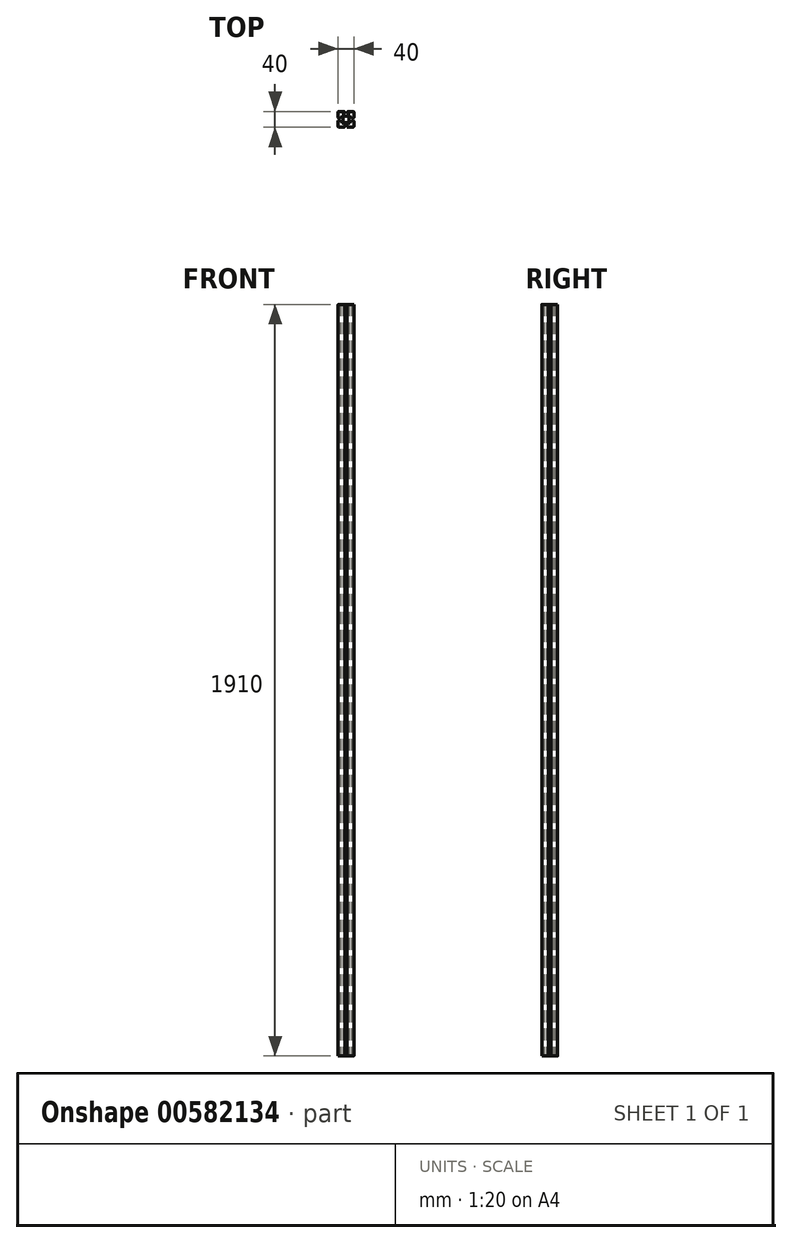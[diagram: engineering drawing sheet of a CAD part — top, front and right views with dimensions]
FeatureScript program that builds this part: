
annotation { "Feature Type Name" : "Feature", "Feature Type Description" : "" }
export const myFeature = defineFeature(function(context is Context, id is Id, definition is map)
    precondition{}
    {
        {
            var Q0;
            Q0=qCreatedBy(makeId("Top.planeOp"),FACE);
            var sketch = newSketch(context, id + "F0", { "sketchPlane" : qUnion([Q0])});
            skLineSegment(sketch, "E0.bottom", {"start": v(20, 20) * mm, "end": v(3, 20) * mm});
            skLineSegment(sketch, "E0.top", {"start": v(20, -20) * mm, "end": v(3, -20) * mm});
            skLineSegment(sketch, "E0.left", {"start": v(20, 20) * mm, "end": v(20, 3) * mm});
            skLineSegment(sketch, "E0.right", {"start": v(-20, 20) * mm, "end": v(-20, 3) * mm});
            skPoint(sketch, "E0.middle", {"position": v(0, 0) * mm});
            skLineSegment(sketch, "E1.left", {"start": v(3, 14) * mm, "end": v(3, 20) * mm});
            skLineSegment(sketch, "E1.right", {"start": v(-3, 14) * mm, "end": v(-3, 20) * mm});
            skPoint(sketch, "E1.middle", {"position": v(0, 20) * mm});
            skLineSegment(sketch, "E2.bottom", {"start": v(-6, 14) * mm, "end": v(-3, 14) * mm});
            skLineSegment(sketch, "E2.top", {"start": v(-6, 8) * mm, "end": v(6, 8) * mm});
            skLineSegment(sketch, "E2.left", {"start": v(-6, 14) * mm, "end": v(-6, 8) * mm});
            skLineSegment(sketch, "E2.right", {"start": v(6, 14) * mm, "end": v(6, 8) * mm});
            skPoint(sketch, "E2.middle", {"position": v(0, 11) * mm});
            skLineSegment(sketch, "E3.bottom", {"start": v(14, 3) * mm, "end": v(20, 3) * mm});
            skLineSegment(sketch, "E3.top", {"start": v(14, -3) * mm, "end": v(20, -3) * mm});
            skPoint(sketch, "E3.middle", {"position": v(20, 0) * mm});
            skLineSegment(sketch, "E4.bottom", {"start": v(14, 6) * mm, "end": v(8, 6) * mm});
            skLineSegment(sketch, "E4.top", {"start": v(14, -6) * mm, "end": v(8, -6) * mm});
            skLineSegment(sketch, "E4.left", {"start": v(14, 6) * mm, "end": v(14, 3) * mm});
            skLineSegment(sketch, "E4.right", {"start": v(8, 6) * mm, "end": v(8, -6) * mm});
            skPoint(sketch, "E4.middle", {"position": v(11, 0) * mm});
            skPoint(sketch, "E4.middle.positionSnap0", {"position": v(14, 0) * mm});
            skPoint(sketch, "E4.centerSnap0", {"position": v(14, 0) * mm});
            skLineSegment(sketch, "E5.left", {"start": v(3.1, -14) * mm, "end": v(3, -20) * mm});
            skLineSegment(sketch, "E5.right", {"start": v(-2.9, -14) * mm, "end": v(-3, -20) * mm});
            skPoint(sketch, "E5.middle", {"position": v(0, -20) * mm});
            skLineSegment(sketch, "E6.bottom", {"start": v(6, -14) * mm, "end": v(3.1, -14) * mm});
            skLineSegment(sketch, "E6.top", {"start": v(6, -8) * mm, "end": v(-6, -8) * mm});
            skLineSegment(sketch, "E6.left", {"start": v(6, -14) * mm, "end": v(6, -8) * mm});
            skLineSegment(sketch, "E6.right", {"start": v(-6, -14) * mm, "end": v(-6, -8) * mm});
            skPoint(sketch, "E6.middle", {"position": v(0, -11) * mm});
            skLineSegment(sketch, "E7.bottom", {"start": v(-14, -3) * mm, "end": v(-20, -3) * mm});
            skLineSegment(sketch, "E7.top", {"start": v(-14, 3) * mm, "end": v(-20, 3) * mm});
            skPoint(sketch, "E7.middle", {"position": v(-20, 0) * mm});
            skLineSegment(sketch, "E8.bottom", {"start": v(-14, 6) * mm, "end": v(-8, 6) * mm});
            skLineSegment(sketch, "E8.top", {"start": v(-14, -6) * mm, "end": v(-8, -6) * mm});
            skLineSegment(sketch, "E8.left", {"start": v(-14, 6) * mm, "end": v(-14, 3) * mm});
            skLineSegment(sketch, "E8.right", {"start": v(-8, 6) * mm, "end": v(-8, -6) * mm});
            skPoint(sketch, "E8.middle", {"position": v(-11, 0) * mm});
            skPoint(sketch, "E8.cornerSnap0", {"position": v(-14, 0) * mm});
            skPoint(sketch, "E9.orphan", {"position": v(-3, 26) * mm});
            skPoint(sketch, "E10.orphan", {"position": v(3, 26) * mm});
            skLineSegment(sketch, "E11.trimOffspring", {"start": v(-3, 20) * mm, "end": v(-20, 20) * mm});
            skLineSegment(sketch, "E12.trimOffspring", {"start": v(3, 14) * mm, "end": v(6, 14) * mm});
            skLineSegment(sketch, "E13.trimOffspring", {"start": v(14, -3) * mm, "end": v(14, -6) * mm});
            skLineSegment(sketch, "E14.trimOffspring", {"start": v(20, -3) * mm, "end": v(20, -20) * mm});
            skPoint(sketch, "E3.right.start.orphan", {"position": v(26, 3) * mm});
            skPoint(sketch, "E15.orphan", {"position": v(26, -3) * mm});
            skLineSegment(sketch, "E16.trimOffspring", {"start": v(-14, -3) * mm, "end": v(-14, -6) * mm});
            skPoint(sketch, "E7.right.end.orphan", {"position": v(-26, 3) * mm});
            skPoint(sketch, "E17.orphan", {"position": v(-26, -3) * mm});
            skLineSegment(sketch, "E18.trimOffspring", {"start": v(-20, -3) * mm, "end": v(-20, -20) * mm});
            skLineSegment(sketch, "E19.trimOffspring", {"start": v(-2.9, -14) * mm, "end": v(-6, -14) * mm});
            skLineSegment(sketch, "E20.trimOffspring", {"start": v(-3, -20) * mm, "end": v(-20, -20) * mm});
            skPoint(sketch, "E21.orphan", {"position": v(-3.1, -26) * mm});
            skPoint(sketch, "E22.orphan", {"position": v(2.9, -26) * mm});
            skSolve(sketch);
        }
        {
            var Q0;
            Q0=qSketchRegion(id+"F0",true);
            extrude(context, id + "F1", {"entities" : qUnion([Q0]), "depth" : 1910 * mm, "offsetDistance" : 25 * mm});
        }
        {
            var Q0;
            Q0=makeQuery(id+"F1.opExtrude","SWEPT_EDGE",EDGE,{"disambiguationData":[OSD([sQuery(id+"F0.wireOp",EDGE,"E0.left"),sQuery(id+"F0.wireOp",EDGE,"E3.bottom")])]});
            var Q1;
            Q1=makeQuery(id+"F1.opExtrude","SWEPT_EDGE",EDGE,{"disambiguationData":[OSD([sQuery(id+"F0.wireOp",EDGE,"E0.bottom"),sQuery(id+"F0.wireOp",EDGE,"E0.left")])]});
            var Q2;
            Q2=makeQuery(id+"F1.opExtrude","SWEPT_EDGE",EDGE,{"disambiguationData":[OSD([sQuery(id+"F0.wireOp",EDGE,"E0.top"),sQuery(id+"F0.wireOp",EDGE,"E14.trimOffspring")])]});
            var Q3;
            Q3=makeQuery(id+"F1.opExtrude","SWEPT_EDGE",EDGE,{"disambiguationData":[OSD([sQuery(id+"F0.wireOp",EDGE,"E3.top"),sQuery(id+"F0.wireOp",EDGE,"E14.trimOffspring")])]});
            var Q4;
            Q4=makeQuery(id+"F1.opExtrude","SWEPT_EDGE",EDGE,{"disambiguationData":[OSD([sQuery(id+"F0.wireOp",EDGE,"E5.right"),sQuery(id+"F0.wireOp",EDGE,"E20.trimOffspring")])]});
            var Q5;
            Q5=makeQuery(id+"F1.opExtrude","SWEPT_EDGE",EDGE,{"disambiguationData":[OSD([sQuery(id+"F0.wireOp",EDGE,"E1.right"),sQuery(id+"F0.wireOp",EDGE,"E11.trimOffspring")])]});
            var Q6;
            Q6=makeQuery(id+"F1.opExtrude","SWEPT_EDGE",EDGE,{"disambiguationData":[OSD([sQuery(id+"F0.wireOp",EDGE,"E0.bottom"),sQuery(id+"F0.wireOp",EDGE,"E1.left")])]});
            var Q7;
            Q7=makeQuery(id+"F1.opExtrude","SWEPT_EDGE",EDGE,{"disambiguationData":[OSD([sQuery(id+"F0.wireOp",EDGE,"E0.right"),sQuery(id+"F0.wireOp",EDGE,"E11.trimOffspring")])]});
            var Q8;
            Q8=makeQuery(id+"F1.opExtrude","SWEPT_EDGE",EDGE,{"disambiguationData":[OSD([sQuery(id+"F0.wireOp",EDGE,"E7.bottom"),sQuery(id+"F0.wireOp",EDGE,"E18.trimOffspring")])]});
            var Q9;
            Q9=makeQuery(id+"F1.opExtrude","SWEPT_EDGE",EDGE,{"disambiguationData":[OSD([sQuery(id+"F0.wireOp",EDGE,"E0.right"),sQuery(id+"F0.wireOp",EDGE,"E7.top")])]});
            var Q10;
            Q10=makeQuery(id+"F1.opExtrude","SWEPT_EDGE",EDGE,{"disambiguationData":[OSD([sQuery(id+"F0.wireOp",EDGE,"E18.trimOffspring"),sQuery(id+"F0.wireOp",EDGE,"E20.trimOffspring")])]});
            fillet(context, id + "F2", {"entities" : qUnion([Q0, Q1, Q2, Q3, Q4, Q5, Q6, Q7, Q8, Q9, Q10]), "radius" : 2 * mm, "tangentPropagation" : true, "allowEdgeOverflow" : false});
        }
    });
